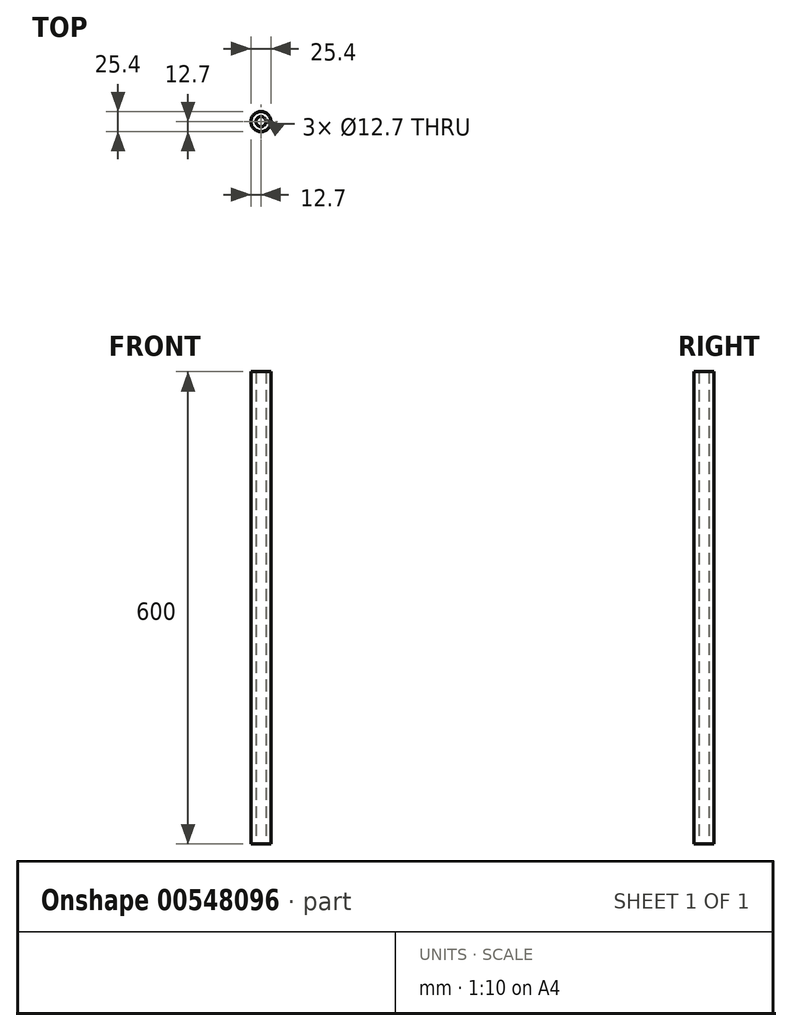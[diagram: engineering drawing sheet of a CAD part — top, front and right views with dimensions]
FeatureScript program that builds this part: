
annotation { "Feature Type Name" : "Feature", "Feature Type Description" : "" }
export const myFeature = defineFeature(function(context is Context, id is Id, definition is map)
    precondition{}
    {
        {
            var Q0;
            Q0=qCreatedBy(makeId("Top.planeOp"),FACE);
            var sketch = newSketch(context, id + "F0", { "sketchPlane" : qUnion([Q0])});
            skCircle(sketch, "E0", {"center": v(0, 0) * mm, "radius": 12.7 * mm});
            skCircle(sketch, "E1", {"center": v(0, 0) * mm, "radius": 6.35 * mm});
            skSolve(sketch);
        }
        {
            var Q0;
            Q0 = qSketchRegion(id + "F0", true);
            extrude(context, id + "F1", {"entities" : qUnion([Q0]), "depth" : 600 * mm, "offsetDistance" : 25.4 * mm});
        }
    });
